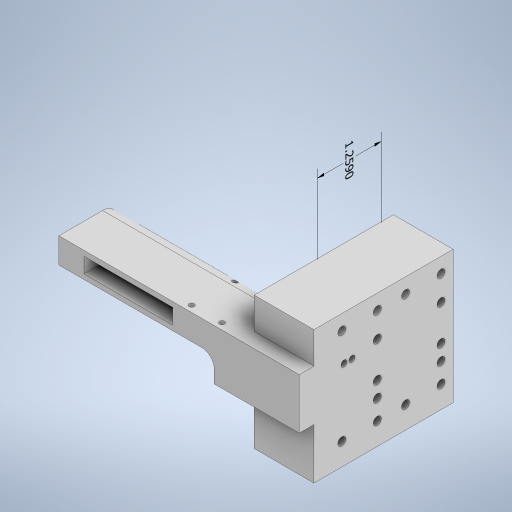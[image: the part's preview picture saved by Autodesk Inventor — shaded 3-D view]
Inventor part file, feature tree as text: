
AUTODESK INVENTOR PART (.ipt)
format: ipt  version: 2024.2 (Build 282272000, 272)  size: 523,776 bytes
history: native  units: in
note: dims shown in document units (in); Inventor stores cm internally (conversion verified against a paired STEP export)
features: extrude x20, sketch x20, projected_geometry x6, fillet x3, other x2
ambient origin geometry x8: Origin, YZ Plane, XZ Plane, XY Plane, X Axis, Y Axis, Z Axis, Center Point
bodies: Solid1 (feature_tree)
feature tree (51):
  other  "Annotations"
  extrude  "Extrusion1"  Depth=2.0in
  extrude  "Extrusion2"  Depth=1.5in
  extrude  "Extrusion3"  Depth=1.5in TaperAngle=0.0deg
  extrude  "Extrusion4"  Depth=0.5in
  fillet  "Fillet1"  Radius=0.25in
  extrude  "Extrusion5"  Depth=1.5in
  extrude  "Extrusion7"  Depth=0.118in
  extrude  "Extrusion8"  TaperAngle=0.0deg  [1 undecoded]
  extrude  "Extrusion9"  Depth=0.539in TaperAngle=0.0deg
  extrude  "Extrusion10"  Depth=0.787in
  extrude  "Extrusion11"  Depth=0.5in TaperAngle=0.0deg
  extrude  "Extrusion12"  Depth=0.157in
  extrude  "Extrusion13"  Depth=0.157in
  extrude  "Extrusion14"  Depth=1.259in
  extrude  "Extrusion15"  Depth=0.25in
  extrude  "Extrusion16"  TaperAngle=0.0deg  [1 undecoded]
  extrude  "Extrusion17"  Depth=0.1in
  extrude  "Extrusion18"  Depth=0.1in
  extrude  "Extrusion19"  Depth=0.6in
  extrude  "Extrusion20"  Depth=0.85in
  extrude  "Extrusion21"  Depth=0.15in
  fillet  "Fillet4"  [1 undecoded]
  fillet  "Fillet5"  [1 undecoded]
  sketch  "Sketch1"  dims[d0=2.75in d1=2.0in]
  sketch  "Sketch2"  dims[d2=1.5in d3=0.0in d4=1.375in]
  sketch  "Sketch3"  dims[d5=1.57in d6=1.5in d7=0.0in]
  sketch  "Sketch4"  dims[d9=0.5in d10=0.5in d11=0.25in]
  sketch  "Sketch5"  dims[d12=1.5in d13=0.0in d14=0.157in]
  projected_geometry  "Projected Loop1"
  sketch  "Sketch9"  dims[d15=0.118in d16=0.118in]
  projected_geometry  "Projected Loop2"
  sketch  "Sketch10"  dims[d17=0.125in d18=0.0in d19=0.0in]
  sketch  "Sketch11"  dims[d20=0.125in d21=0.539in d22=0.0in]
  sketch  "Sketch12"  dims[d23=0.2in d24=0.787in]
  sketch  "Sketch13"  dims[d25=1.069in d41=0.5in d42=0.0in]
  sketch  "Sketch14"  dims[d43=0.157in d44=0.157in]
  sketch  "Sketch15"  dims[d45=0.157in d46=0.157in]
  sketch  "Sketch16"  dims[d47=1.259in d48=1.259in]
  projected_geometry  "Projected Loop3"
  sketch  "Sketch17"  dims[d49=0.25in d50=0.25in]
  sketch  "Sketch18"  dims[d51=0.0in d52=0.0in d53=0.0in]
  projected_geometry  "Projected Loop4"
  sketch  "Sketch19"  dims[d54=0.1in d55=0.1in]
  projected_geometry  "Projected Loop5"
  sketch  "Sketch20"  dims[d56=0.1in d57=0.1in]
  projected_geometry  "Projected Loop6"
  sketch  "Sketch21"  dims[d58=0.0in d59=0.6in]
  sketch  "Sketch22"  dims[d60=0.6in d61=0.85in]
  sketch  "Sketch23"  dims[d62=0.0in d63=0.5in d64=0.0in d65=0.0in d66=0.0in d67=1.75in d68=0.625in d69=0.0in d70=0.157in d71=0.157in d72=0.49in d73=0.49in d74=0.0in d75=0.157in d76=0.157in d77=1.0in d78=0.0in d79=0.5in d80=0.0in d81=0.157in d82=0.0in d83=1.889in d84=1.889in d85=0.0in d86=0.0in d87=2.0in d88=0.0in d89=0.1in d90=0.1in d91=0.1in d92=0.1in d93=0.6in d94=0.6in d95=0.85in d96=2.25in d97=0.125in d98=0.125in d99=0.0in d100=0.0in d101=0.0in d102=0.5in d103=0.0in d104=1.0in d105=0.0in d106=1.0in d107=0.0in d109=0.241in d110=0.157in d111=0.157in d112=1.259in d113=0.7in d114=1.0in d115=0.0in d116=0.157in d117=1.259in d118=0.0in d119=0.0in d120=1.889in d121=0.0in d122=0.0in d123=0.1in d124=0.1in d125=0.5in d126=0.0in d127=0.0in d128=1.75in d129=0.3in d130=0.15in d108=1.259in]
  other  "Linear Dimension 1"
note: 4 required parameter values undecoded (feature->parameter linkage not recoverable at this tier; creation-order binding heuristic only, values carry confidence <= 0.55)
